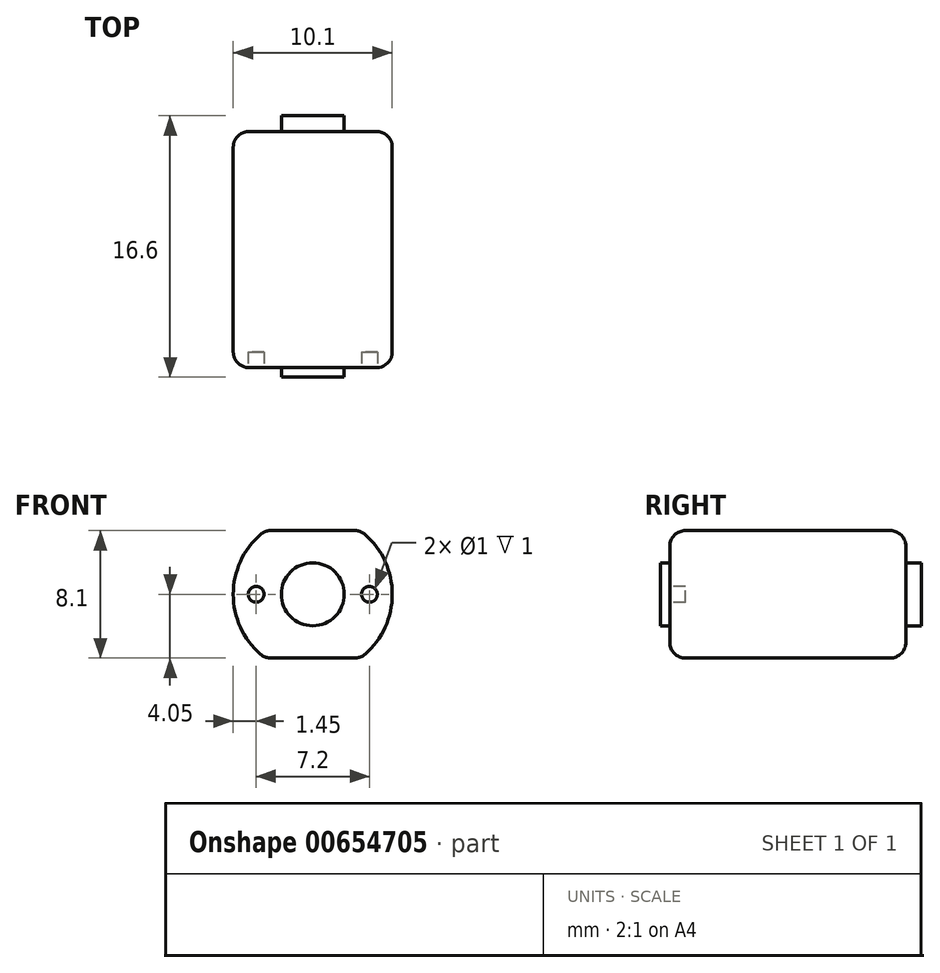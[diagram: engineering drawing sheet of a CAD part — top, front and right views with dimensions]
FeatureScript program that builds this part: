
annotation { "Feature Type Name" : "Feature", "Feature Type Description" : "" }
export const myFeature = defineFeature(function(context is Context, id is Id, definition is map)
    precondition{}
    {
        {
            var Q0;
            Q0=qCreatedBy(makeId("Front.planeOp"),FACE);
            var sketch = newSketch(context, id + "F0", { "sketchPlane" : qUnion([Q0])});
            skArc(sketch, "E0", {"start": v(-3.02, 4.05) * mm, "mid": v(-5.05, 0) * mm, "end": v(-3.02, -4.05) * mm});
            skLineSegment(sketch, "E1.bottom", {"start": v(-3.02, 4.05) * mm, "end": v(3.02, 4.05) * mm});
            skLineSegment(sketch, "E1.top", {"start": v(-3.02, -4.05) * mm, "end": v(3.02, -4.05) * mm});
            skLineSegment(sketch, "E1.left", {"start": v(-3.02, 4.05) * mm, "end": v(-3.02, -4.05) * mm});
            skLineSegment(sketch, "E1.right", {"start": v(3.02, 4.05) * mm, "end": v(3.02, -4.05) * mm});
            skArc(sketch, "E2.trimOffspring", {"start": v(3.02, -4.05) * mm, "mid": v(5.05, 0) * mm, "end": v(3.02, 4.05) * mm});
            skSolve(sketch);
        }
        {
            var Q0;
            Q0=makeQuery(id+"F0.imprint","IMPRINT",FACE,{"disambiguationData":[TD([[makeQuery(id+"F0.imprint","IMPRINT",EDGE,{"derivedFrom":sQuery(id+"F0.wireOp",EDGE,"E1.bottom")}),-1.0]])]});
            var Q1;
            Q1=makeQuery(id+"F0.imprint","IMPRINT",FACE,{"disambiguationData":[TD([[makeQuery(id+"F0.imprint","IMPRINT",EDGE,{"derivedFrom":sQuery(id+"F0.wireOp",EDGE,"E1.right")}),1.0]])]});
            var Q2;
            Q2=makeQuery(id+"F0.imprint","IMPRINT",FACE,{"disambiguationData":[TD([[makeQuery(id+"F0.imprint","IMPRINT",EDGE,{"derivedFrom":sQuery(id+"F0.wireOp",EDGE,"E0")}),1.0]])]});
            extrude(context, id + "F1", {"entities" : qUnion([Q0, Q1, Q2]), "endBound" : BoundingType.SYMMETRIC, "depth" : 15 * mm});
        }
        {
            var Q0;
            Q0=makeQuery(id+"F1.opExtrude","CAP_FACE",FACE,{"disambiguationData":[OSD([sQuery(id+"F0.wireOp",EDGE,"E0"),sQuery(id+"F0.wireOp",EDGE,"E1.bottom"),sQuery(id+"F0.wireOp",EDGE,"E1.top"),sQuery(id+"F0.wireOp",EDGE,"E2.trimOffspring")])],"isStart":false});
            var sketch = newSketch(context, id + "F2", { "sketchPlane" : qUnion([Q0])});
            skCircle(sketch, "E3", {"center": v(0, 0) * mm, "radius": 2 * mm});
            skSolve(sketch);
        }
        {
            var Q0;
            Q0=makeQuery(id+"F2.imprint","IMPRINT",FACE,{"disambiguationData":[TD([[makeQuery(id+"F2.imprint","IMPRINT",EDGE,{"derivedFrom":sQuery(id+"F2.wireOp",EDGE,"E3")}),1.0]])]});
            extrude(context, id + "F3", {"entities" : qUnion([Q0]), "operationType" : NewBodyOperationType.ADD, "depth" : 0.6 * mm});
        }
        {
            var Q0;
            Q0=makeQuery(id+"F1.opExtrude","CAP_FACE",FACE,{"disambiguationData":[OSD([sQuery(id+"F0.wireOp",EDGE,"E0"),sQuery(id+"F0.wireOp",EDGE,"E1.bottom"),sQuery(id+"F0.wireOp",EDGE,"E1.top"),sQuery(id+"F0.wireOp",EDGE,"E2.trimOffspring")])],"isStart":true});
            var sketch = newSketch(context, id + "F4", { "sketchPlane" : qUnion([Q0])});
            skCircle(sketch, "E4", {"center": v(0, 0) * mm, "radius": 2 * mm});
            skSolve(sketch);
        }
        {
            var Q0;
            Q0=makeQuery(id+"F4.imprint","IMPRINT",FACE,{"disambiguationData":[TD([[makeQuery(id+"F4.imprint","IMPRINT",EDGE,{"derivedFrom":sQuery(id+"F4.wireOp",EDGE,"E4")}),1.0]])]});
            extrude(context, id + "F5", {"entities" : qUnion([Q0]), "operationType" : NewBodyOperationType.ADD, "depth" : 1 * mm});
        }
        {
            var Q0;
            Q0=makeQuery(id+"F1.opExtrude","CAP_FACE",FACE,{"disambiguationData":[OSD([sQuery(id+"F0.wireOp",EDGE,"E0"),sQuery(id+"F0.wireOp",EDGE,"E1.bottom"),sQuery(id+"F0.wireOp",EDGE,"E1.top"),sQuery(id+"F0.wireOp",EDGE,"E2.trimOffspring")])],"isStart":false});
            var sketch = newSketch(context, id + "F6", { "sketchPlane" : qUnion([Q0])});
            skLineSegment(sketch, "E5", {"start": v(5.05, 0) * mm, "end": v(4.1, 0) * mm});
            skCircle(sketch, "E6", {"center": v(-3.6, 0) * mm, "radius": 0.5 * mm});
            skCircle(sketch, "E7", {"center": v(3.6, 0) * mm, "radius": 0.5 * mm});
            skLineSegment(sketch, "E8.trimOffspring", {"start": v(-4.1, 0) * mm, "end": v(-5.05, 0) * mm});
            skSolve(sketch);
        }
        {
            var Q0;
            Q0=qSketchRegion(id+"F6",true);
            extrude(context, id + "F7", {"entities" : qUnion([Q0]), "operationType" : NewBodyOperationType.REMOVE, "oppositeDirection" : true, "depth" : 1 * mm});
        }
        {
            var Q0;
            Q0=makeQuery(id+"F1.opExtrude","SWEPT_EDGE",EDGE,{"disambiguationData":[OSD([sQuery(id+"F0.wireOp",EDGE,"E1.top"),sQuery(id+"F0.wireOp",EDGE,"E1.right"),sQuery(id+"F0.wireOp",EDGE,"E2.trimOffspring")])]});
            var Q1;
            Q1=makeQuery(id+"F1.opExtrude","SWEPT_EDGE",EDGE,{"disambiguationData":[OSD([sQuery(id+"F0.wireOp",EDGE,"E0"),sQuery(id+"F0.wireOp",EDGE,"E1.top"),sQuery(id+"F0.wireOp",EDGE,"E1.left")])]});
            var Q2;
            Q2=makeQuery(id+"F1.opExtrude","SWEPT_EDGE",EDGE,{"disambiguationData":[OSD([sQuery(id+"F0.wireOp",EDGE,"E1.bottom"),sQuery(id+"F0.wireOp",EDGE,"E1.right"),sQuery(id+"F0.wireOp",EDGE,"E2.trimOffspring")])]});
            var Q3;
            Q3=makeQuery(id+"F1.opExtrude","SWEPT_EDGE",EDGE,{"disambiguationData":[OSD([sQuery(id+"F0.wireOp",EDGE,"E0"),sQuery(id+"F0.wireOp",EDGE,"E1.bottom"),sQuery(id+"F0.wireOp",EDGE,"E1.left")])]});
            var Q4;
            Q4=makeQuery(id+"F1.opExtrude","CAP_EDGE",EDGE,{"disambiguationData":[OSD([sQuery(id+"F0.wireOp",EDGE,"E1.bottom")])],"isStart":false});
            var Q5;
            Q5=makeQuery(id+"F1.opExtrude","CAP_EDGE",EDGE,{"disambiguationData":[OSD([sQuery(id+"F0.wireOp",EDGE,"E0")])],"isStart":false});
            var Q6;
            Q6=makeQuery(id+"F1.opExtrude","CAP_EDGE",EDGE,{"disambiguationData":[OSD([sQuery(id+"F0.wireOp",EDGE,"E2.trimOffspring")])],"isStart":false});
            var Q7;
            Q7=makeQuery(id+"F1.opExtrude","CAP_EDGE",EDGE,{"disambiguationData":[OSD([sQuery(id+"F0.wireOp",EDGE,"E1.top")])],"isStart":false});
            var Q8;
            Q8=makeQuery(id+"F1.opExtrude","CAP_EDGE",EDGE,{"disambiguationData":[OSD([sQuery(id+"F0.wireOp",EDGE,"E0")])],"isStart":true});
            var Q9;
            Q9=makeQuery(id+"F1.opExtrude","CAP_EDGE",EDGE,{"disambiguationData":[OSD([sQuery(id+"F0.wireOp",EDGE,"E1.bottom")])],"isStart":true});
            var Q10;
            Q10=makeQuery(id+"F1.opExtrude","CAP_EDGE",EDGE,{"disambiguationData":[OSD([sQuery(id+"F0.wireOp",EDGE,"E2.trimOffspring")])],"isStart":true});
            var Q11;
            Q11=makeQuery(id+"F1.opExtrude","CAP_EDGE",EDGE,{"disambiguationData":[OSD([sQuery(id+"F0.wireOp",EDGE,"E1.top")])],"isStart":true});
            fillet(context, id + "F8", {"entities" : qUnion([Q0, Q1, Q2, Q3, Q4, Q5, Q6, Q7, Q8, Q9, Q10, Q11]), "radius" : 1 * mm, "tangentPropagation" : true, "allowEdgeOverflow" : false});
        }
    });
